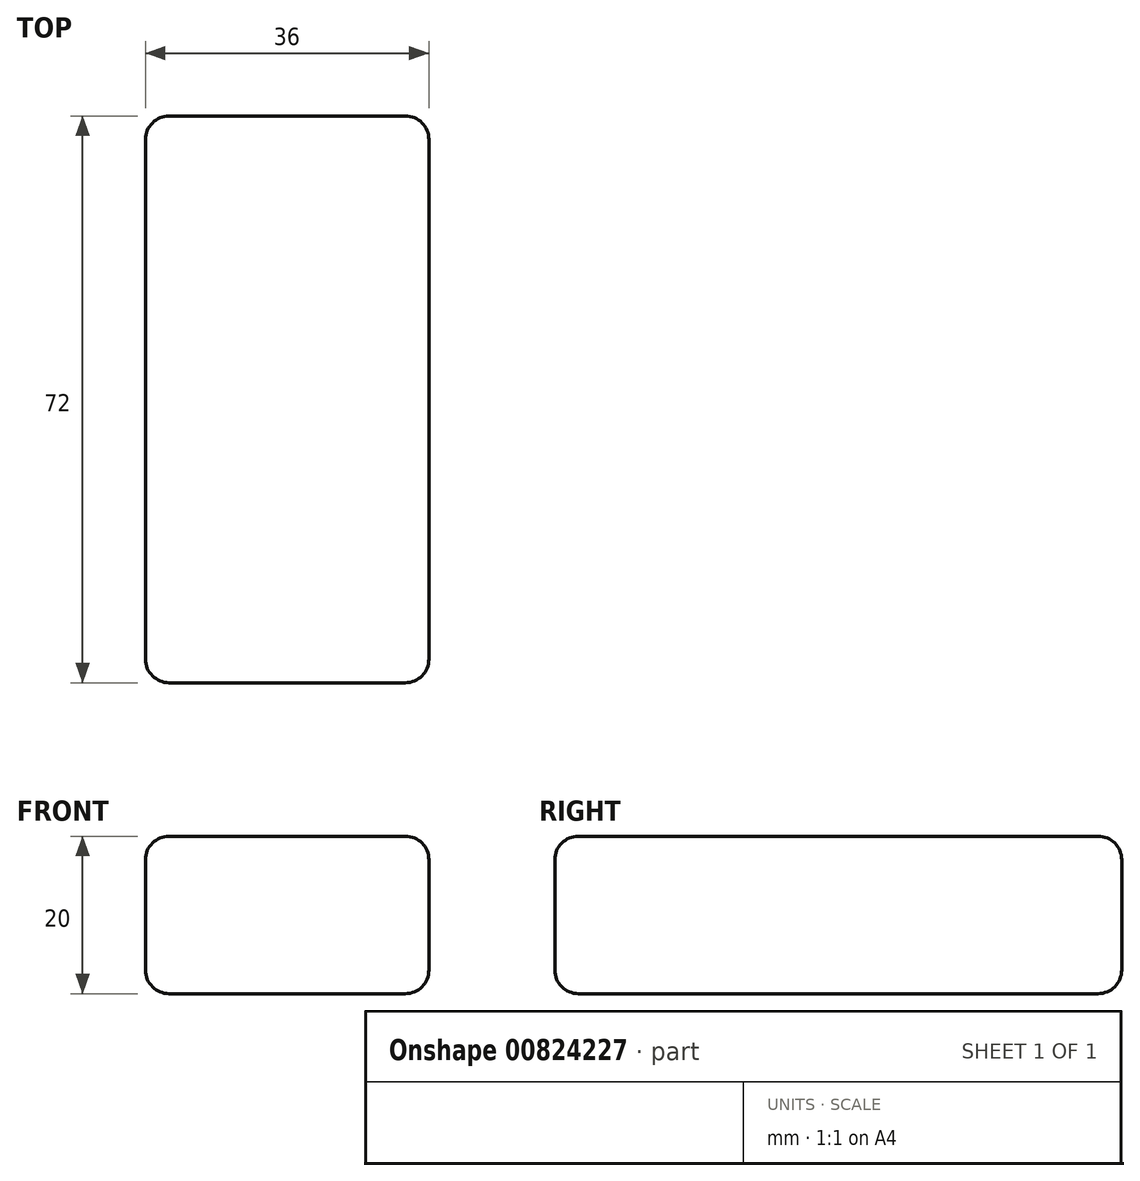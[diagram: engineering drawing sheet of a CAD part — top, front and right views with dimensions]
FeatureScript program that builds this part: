
annotation { "Feature Type Name" : "Feature", "Feature Type Description" : "" }
export const myFeature = defineFeature(function(context is Context, id is Id, definition is map)
    precondition{}
    {
        {
            var Q0;
            Q0=qCreatedBy(makeId("Top.planeOp"),FACE);
            var sketch = newSketch(context, id + "F0", { "sketchPlane" : qUnion([Q0])});
            skLineSegment(sketch, "E0.bottom", {"start": v(18, -36) * mm, "end": v(-18, -36) * mm});
            skLineSegment(sketch, "E0.top", {"start": v(18, 36) * mm, "end": v(-18, 36) * mm});
            skLineSegment(sketch, "E0.left", {"start": v(18, -36) * mm, "end": v(18, 36) * mm});
            skLineSegment(sketch, "E0.right", {"start": v(-18, -36) * mm, "end": v(-18, 36) * mm});
            skPoint(sketch, "E0.middle", {"position": v(0, 0) * mm});
            skSolve(sketch);
        }
        {
            var Q0;
            Q0=makeQuery(id+"F0.imprint","IMPRINT",FACE,{"disambiguationData":[TD([[makeQuery(id+"F0.imprint","IMPRINT",EDGE,{"derivedFrom":sQuery(id+"F0.wireOp",EDGE,"E0.bottom")}),-1.0]])]});
            extrude(context, id + "F1", {"entities" : qUnion([Q0]), "depth" : 20 * mm, "offsetDistance" : 25 * mm});
        }
        {
            var Q0;
            Q0=makeQuery(id+"F1.opExtrude","CAP_FACE",FACE,{"disambiguationData":[OSD([sQuery(id+"F0.wireOp",EDGE,"E0.bottom"),sQuery(id+"F0.wireOp",EDGE,"E0.top"),sQuery(id+"F0.wireOp",EDGE,"E0.left"),sQuery(id+"F0.wireOp",EDGE,"E0.right")])],"isStart":false});
            var Q1;
            Q1=makeQuery(id+"F1.opExtrude","CAP_FACE",FACE,{"disambiguationData":[OSD([sQuery(id+"F0.wireOp",EDGE,"E0.bottom"),sQuery(id+"F0.wireOp",EDGE,"E0.top"),sQuery(id+"F0.wireOp",EDGE,"E0.left"),sQuery(id+"F0.wireOp",EDGE,"E0.right")])],"isStart":true});
            var Q2;
            Q2=makeQuery(id+"F1.opExtrude","SWEPT_FACE",FACE,{"disambiguationData":[OSD([sQuery(id+"F0.wireOp",EDGE,"E0.left")])]});
            var Q3;
            Q3=makeQuery(id+"F1.opExtrude","SWEPT_FACE",FACE,{"disambiguationData":[OSD([sQuery(id+"F0.wireOp",EDGE,"E0.right")])]});
            fillet(context, id + "F2", {"entities" : qUnion([Q0, Q1, Q2, Q3]), "radius" : 3 * mm, "tangentPropagation" : true, "allowEdgeOverflow" : false});
        }
    });
